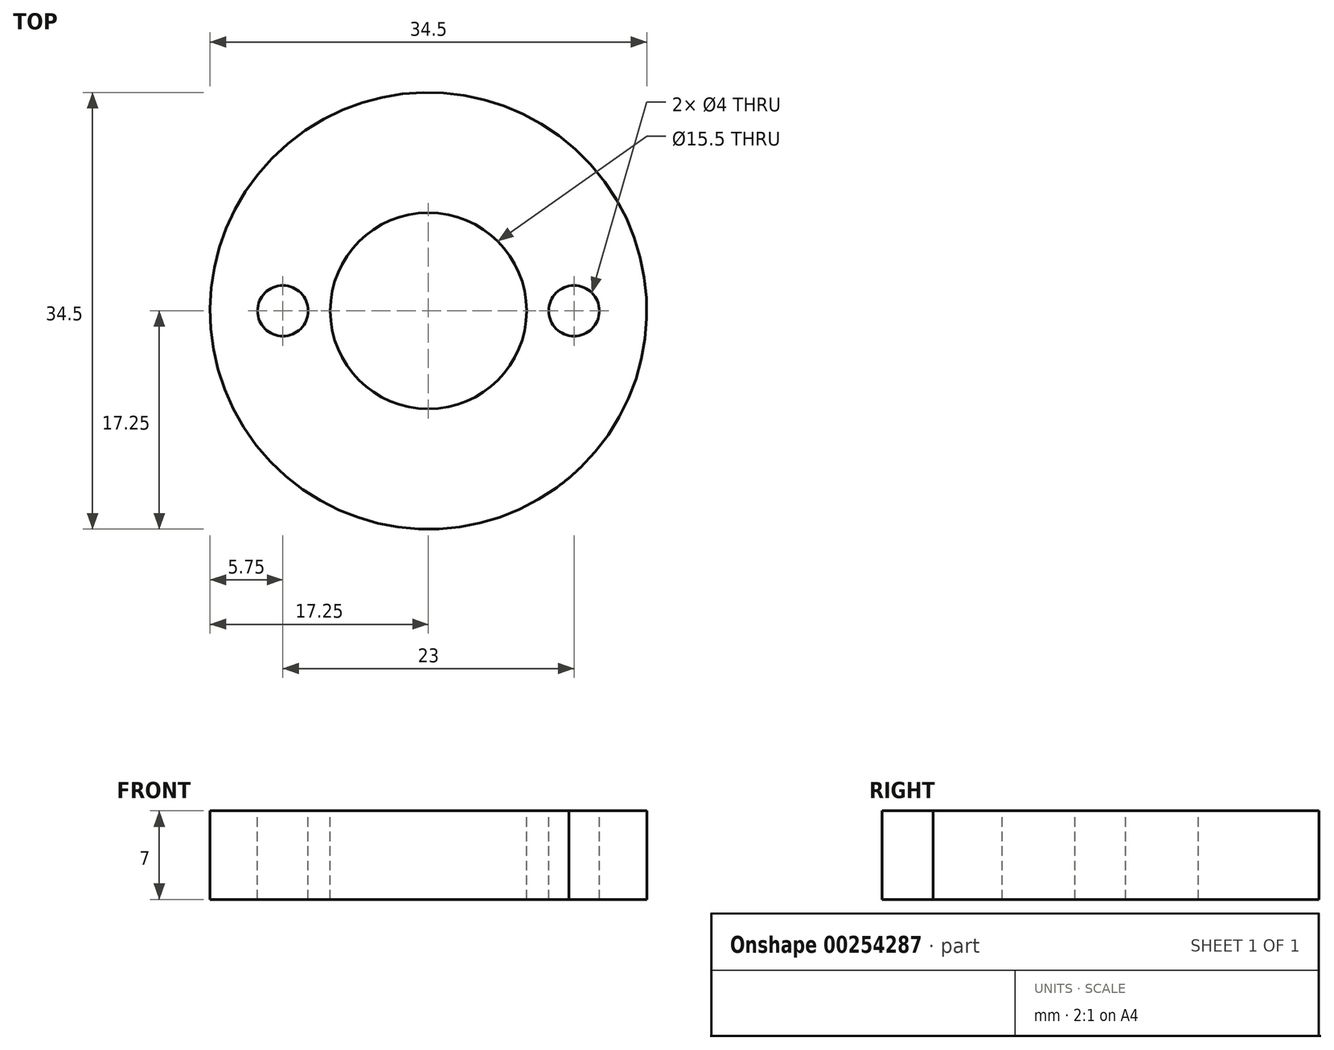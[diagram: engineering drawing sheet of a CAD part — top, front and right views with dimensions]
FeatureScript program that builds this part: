
annotation { "Feature Type Name" : "Feature", "Feature Type Description" : "" }
export const myFeature = defineFeature(function(context is Context, id is Id, definition is map)
    precondition{}
    {
        {
            var Q0;
            Q0=qCreatedBy(makeId("Top.planeOp"),FACE);
            var sketch = newSketch(context, id + "F0", { "sketchPlane" : qUnion([Q0])});
            skCircle(sketch, "E0", {"center": v(0, 0) * mm, "radius": 17.25 * mm});
            skLineSegment(sketch, "E1", {"start": v(0, 25.78) * mm, "end": v(0, -27.7) * mm});
            skLineSegment(sketch, "E2", {"start": v(-26.27, 0) * mm, "end": v(30.25, 0) * mm});
            skPoint(sketch, "E3.visualSharp", {"position": v(0, 20.27) * mm});
            skArc(sketch, "E3.filletArc", {"start": v(0.28, 19.56) * mm, "mid": v(0, 19.75) * mm, "end": v(-0.28, 19.56) * mm});
            skLineSegment(sketch, "E4", {"start": v(0, 17.25) * mm, "end": v(0, 19.75) * mm});
            skFitSpline(sketch, "E5", {"points": [v(-1.2, 17.2) * mm, v(-0.94, 18.19) * mm, v(-0.28, 19.56) * mm], "startDerivative": vector(0.47, 2.11) * mm, "endDerivative": vector(1.5, 2.4) * mm});
            skFitSpline(sketch, "E6.MirrorCS", {"points": [v(1.2, 17.2) * mm, v(0.94, 18.19) * mm, v(0.28, 19.56) * mm], "startDerivative": vector(-0.47, 2.11) * mm, "endDerivative": vector(-1.5, 2.4) * mm});
            skFitSpline(sketch, "E7", {"points": [v(-1.2, 17.2) * mm, v(0, 17.25) * mm, v(1.2, 17.2) * mm], "startDerivative": vector(2.41, 0.13) * mm, "endDerivative": vector(2.41, -0.13) * mm});
            skSolve(sketch);
        }
        {
            var Q0;
            {var subQ0=sQuery(id+"F0.wireOp",EDGE,"f5ca5393-df95-4c20-865a-a9dc07791ef0.31.0");Q0=makeQuery(id+"F0.imprint","IMPRINT",FACE,{"disambiguationData":[TD([[makeQuery(id+"F0.imprint","IMPRINT",EDGE,{"derivedFrom":subQ0}),-1.0]])]});}
            var Q1;
            {var subQ0=sQuery(id+"F0.wireOp",EDGE,"f5ca5393-df95-4c20-865a-a9dc07791ef0.29.0");Q1=makeQuery(id+"F0.imprint","IMPRINT",FACE,{"disambiguationData":[TD([[makeQuery(id+"F0.imprint","IMPRINT",EDGE,{"derivedFrom":subQ0}),-1.0]])]});}
            var Q2;
            {var subQ0=sQuery(id+"F0.wireOp",EDGE,"f5ca5393-df95-4c20-865a-a9dc07791ef0.30.0");Q2=makeQuery(id+"F0.imprint","IMPRINT",FACE,{"disambiguationData":[TD([[makeQuery(id+"F0.imprint","IMPRINT",EDGE,{"derivedFrom":subQ0}),-1.0]])]});}
            var Q3;
            {var subQ0=sQuery(id+"F0.wireOp",EDGE,"f5ca5393-df95-4c20-865a-a9dc07791ef0.32.0");Q3=makeQuery(id+"F0.imprint","IMPRINT",FACE,{"disambiguationData":[TD([[makeQuery(id+"F0.imprint","IMPRINT",EDGE,{"derivedFrom":subQ0}),-1.0]])]});}
            var Q4;
            {var subQ0=sQuery(id+"F0.wireOp",EDGE,"f5ca5393-df95-4c20-865a-a9dc07791ef0.33.0");Q4=makeQuery(id+"F0.imprint","IMPRINT",FACE,{"disambiguationData":[TD([[makeQuery(id+"F0.imprint","IMPRINT",EDGE,{"derivedFrom":subQ0}),-1.0]])]});}
            var Q5;
            {var subQ0=sQuery(id+"F0.wireOp",EDGE,"f5ca5393-df95-4c20-865a-a9dc07791ef0.34.0");Q5=makeQuery(id+"F0.imprint","IMPRINT",FACE,{"disambiguationData":[TD([[makeQuery(id+"F0.imprint","IMPRINT",EDGE,{"derivedFrom":subQ0}),-1.0]])]});}
            var Q6;
            {var subQ0=sQuery(id+"F0.wireOp",EDGE,"f5ca5393-df95-4c20-865a-a9dc07791ef0.17.0");Q6=makeQuery(id+"F0.imprint","IMPRINT",FACE,{"disambiguationData":[TD([[makeQuery(id+"F0.imprint","IMPRINT",EDGE,{"derivedFrom":subQ0}),-1.0]])]});}
            var Q7;
            {var subQ0=sQuery(id+"F0.wireOp",EDGE,"f5ca5393-df95-4c20-865a-a9dc07791ef0.35.0");Q7=makeQuery(id+"F0.imprint","IMPRINT",FACE,{"disambiguationData":[TD([[makeQuery(id+"F0.imprint","IMPRINT",EDGE,{"derivedFrom":subQ0}),-1.0]])]});}
            var Q8;
            {var subQ0=sQuery(id+"F0.wireOp",EDGE,"E0");var subQ8=makeQuery(id+"F0.imprint","INTERSECT",VERTEX,{"derivedFrom":[subQ0,sQuery(id+"F0.wireOp",EDGE,"5MArOXN8-ynDE-2cLv-vS9q-pv3LUURociim")]});Q8=makeQuery(id+"F0.imprint","IMPRINT",FACE,{"disambiguationData":[TD([[makeQuery(id+"F0.imprint","IMPRINT",EDGE,{"disambiguationData":[TD([[subQ8,1.0]])],"derivedFrom":subQ0}),1.0]])]});}
            var Q9;
            {var subQ0=sQuery(id+"F0.wireOp",EDGE,"fce4d2f8-0420-48c1-941b-f51cf35978c9.1.36.0");Q9=makeQuery(id+"F0.imprint","IMPRINT",FACE,{"disambiguationData":[TD([[makeQuery(id+"F0.imprint","IMPRINT",EDGE,{"derivedFrom":subQ0}),-1.0]])]});}
            var Q10;
            {var subQ0=sQuery(id+"F0.wireOp",EDGE,"f5ca5393-df95-4c20-865a-a9dc07791ef0.24.0");Q10=makeQuery(id+"F0.imprint","IMPRINT",FACE,{"disambiguationData":[TD([[makeQuery(id+"F0.imprint","IMPRINT",EDGE,{"derivedFrom":subQ0}),-1.0]])]});}
            var Q11;
            {var subQ0=sQuery(id+"F0.wireOp",EDGE,"fce4d2f8-0420-48c1-941b-f51cf35978c9.1.37.0");Q11=makeQuery(id+"F0.imprint","IMPRINT",FACE,{"disambiguationData":[TD([[makeQuery(id+"F0.imprint","IMPRINT",EDGE,{"derivedFrom":subQ0}),-1.0]])]});}
            var Q12;
            {var subQ0=sQuery(id+"F0.wireOp",EDGE,"f5ca5393-df95-4c20-865a-a9dc07791ef0.1.0");Q12=makeQuery(id+"F0.imprint","IMPRINT",FACE,{"disambiguationData":[TD([[makeQuery(id+"F0.imprint","IMPRINT",EDGE,{"derivedFrom":subQ0}),-1.0]])]});}
            var Q13;
            {var subQ0=sQuery(id+"F0.wireOp",EDGE,"f5ca5393-df95-4c20-865a-a9dc07791ef0.2.0");Q13=makeQuery(id+"F0.imprint","IMPRINT",FACE,{"disambiguationData":[TD([[makeQuery(id+"F0.imprint","IMPRINT",EDGE,{"derivedFrom":subQ0}),-1.0]])]});}
            var Q14;
            {var subQ0=sQuery(id+"F0.wireOp",EDGE,"f5ca5393-df95-4c20-865a-a9dc07791ef0.3.0");Q14=makeQuery(id+"F0.imprint","IMPRINT",FACE,{"disambiguationData":[TD([[makeQuery(id+"F0.imprint","IMPRINT",EDGE,{"derivedFrom":subQ0}),-1.0]])]});}
            var Q15;
            {var subQ0=sQuery(id+"F0.wireOp",EDGE,"E0");var subQ8=makeQuery(id+"F0.imprint","INTERSECT",VERTEX,{"derivedFrom":[subQ0,sQuery(id+"F0.wireOp",EDGE,"f5ca5393-df95-4c20-865a-a9dc07791ef0.10.2")]});Q15=makeQuery(id+"F0.imprint","IMPRINT",FACE,{"disambiguationData":[TD([[makeQuery(id+"F0.imprint","IMPRINT",EDGE,{"disambiguationData":[TD([[subQ8,1.0]])],"derivedFrom":subQ0}),1.0]])]});}
            var Q16;
            {var subQ0=sQuery(id+"F0.wireOp",EDGE,"f5ca5393-df95-4c20-865a-a9dc07791ef0.18.0");Q16=makeQuery(id+"F0.imprint","IMPRINT",FACE,{"disambiguationData":[TD([[makeQuery(id+"F0.imprint","IMPRINT",EDGE,{"derivedFrom":subQ0}),-1.0]])]});}
            var Q17;
            {var subQ0=sQuery(id+"F0.wireOp",EDGE,"f5ca5393-df95-4c20-865a-a9dc07791ef0.22.0");Q17=makeQuery(id+"F0.imprint","IMPRINT",FACE,{"disambiguationData":[TD([[makeQuery(id+"F0.imprint","IMPRINT",EDGE,{"derivedFrom":subQ0}),-1.0]])]});}
            var Q18;
            {var subQ0=sQuery(id+"F0.wireOp",EDGE,"f5ca5393-df95-4c20-865a-a9dc07791ef0.4.0");Q18=makeQuery(id+"F0.imprint","IMPRINT",FACE,{"disambiguationData":[TD([[makeQuery(id+"F0.imprint","IMPRINT",EDGE,{"derivedFrom":subQ0}),-1.0]])]});}
            var Q19;
            {var subQ0=sQuery(id+"F0.wireOp",EDGE,"E0");var subQ8=makeQuery(id+"F0.imprint","INTERSECT",VERTEX,{"derivedFrom":[subQ0,sQuery(id+"F0.wireOp",EDGE,"f5ca5393-df95-4c20-865a-a9dc07791ef0.19.0")]});Q19=makeQuery(id+"F0.imprint","IMPRINT",FACE,{"disambiguationData":[TD([[makeQuery(id+"F0.imprint","IMPRINT",EDGE,{"disambiguationData":[TD([[subQ8,1.0]])],"derivedFrom":subQ0}),1.0]])]});}
            var Q20;
            {var subQ0=sQuery(id+"F0.wireOp",EDGE,"f5ca5393-df95-4c20-865a-a9dc07791ef0.20.0");Q20=makeQuery(id+"F0.imprint","IMPRINT",FACE,{"disambiguationData":[TD([[makeQuery(id+"F0.imprint","IMPRINT",EDGE,{"derivedFrom":subQ0}),-1.0]])]});}
            var Q21;
            {var subQ0=sQuery(id+"F0.wireOp",EDGE,"f5ca5393-df95-4c20-865a-a9dc07791ef0.23.0");Q21=makeQuery(id+"F0.imprint","IMPRINT",FACE,{"disambiguationData":[TD([[makeQuery(id+"F0.imprint","IMPRINT",EDGE,{"derivedFrom":subQ0}),-1.0]])]});}
            var Q22;
            {var subQ0=sQuery(id+"F0.wireOp",EDGE,"f5ca5393-df95-4c20-865a-a9dc07791ef0.21.0");Q22=makeQuery(id+"F0.imprint","IMPRINT",FACE,{"disambiguationData":[TD([[makeQuery(id+"F0.imprint","IMPRINT",EDGE,{"derivedFrom":subQ0}),-1.0]])]});}
            var Q23;
            {var subQ0=sQuery(id+"F0.wireOp",EDGE,"f5ca5393-df95-4c20-865a-a9dc07791ef0.19.0");Q23=makeQuery(id+"F0.imprint","IMPRINT",FACE,{"disambiguationData":[TD([[makeQuery(id+"F0.imprint","IMPRINT",EDGE,{"derivedFrom":subQ0}),-1.0]])]});}
            var Q24;
            {var subQ0=sQuery(id+"F0.wireOp",EDGE,"f5ca5393-df95-4c20-865a-a9dc07791ef0.15.0");Q24=makeQuery(id+"F0.imprint","IMPRINT",FACE,{"disambiguationData":[TD([[makeQuery(id+"F0.imprint","IMPRINT",EDGE,{"derivedFrom":subQ0}),-1.0]])]});}
            var Q25;
            {var subQ0=sQuery(id+"F0.wireOp",EDGE,"f5ca5393-df95-4c20-865a-a9dc07791ef0.25.0");Q25=makeQuery(id+"F0.imprint","IMPRINT",FACE,{"disambiguationData":[TD([[makeQuery(id+"F0.imprint","IMPRINT",EDGE,{"derivedFrom":subQ0}),-1.0]])]});}
            var Q26;
            {var subQ0=sQuery(id+"F0.wireOp",EDGE,"f5ca5393-df95-4c20-865a-a9dc07791ef0.8.0");Q26=makeQuery(id+"F0.imprint","IMPRINT",FACE,{"disambiguationData":[TD([[makeQuery(id+"F0.imprint","IMPRINT",EDGE,{"derivedFrom":subQ0}),-1.0]])]});}
            var Q27;
            {var subQ0=sQuery(id+"F0.wireOp",EDGE,"f5ca5393-df95-4c20-865a-a9dc07791ef0.9.0");Q27=makeQuery(id+"F0.imprint","IMPRINT",FACE,{"disambiguationData":[TD([[makeQuery(id+"F0.imprint","IMPRINT",EDGE,{"derivedFrom":subQ0}),-1.0]])]});}
            var Q28;
            {var subQ0=sQuery(id+"F0.wireOp",EDGE,"f5ca5393-df95-4c20-865a-a9dc07791ef0.26.0");Q28=makeQuery(id+"F0.imprint","IMPRINT",FACE,{"disambiguationData":[TD([[makeQuery(id+"F0.imprint","IMPRINT",EDGE,{"derivedFrom":subQ0}),-1.0]])]});}
            var Q29;
            {var subQ0=sQuery(id+"F0.wireOp",EDGE,"f5ca5393-df95-4c20-865a-a9dc07791ef0.10.0");Q29=makeQuery(id+"F0.imprint","IMPRINT",FACE,{"disambiguationData":[TD([[makeQuery(id+"F0.imprint","IMPRINT",EDGE,{"derivedFrom":subQ0}),-1.0]])]});}
            var Q30;
            {var subQ0=sQuery(id+"F0.wireOp",EDGE,"f5ca5393-df95-4c20-865a-a9dc07791ef0.27.0");Q30=makeQuery(id+"F0.imprint","IMPRINT",FACE,{"disambiguationData":[TD([[makeQuery(id+"F0.imprint","IMPRINT",EDGE,{"derivedFrom":subQ0}),-1.0]])]});}
            var Q31;
            {var subQ0=sQuery(id+"F0.wireOp",EDGE,"f5ca5393-df95-4c20-865a-a9dc07791ef0.11.0");Q31=makeQuery(id+"F0.imprint","IMPRINT",FACE,{"disambiguationData":[TD([[makeQuery(id+"F0.imprint","IMPRINT",EDGE,{"derivedFrom":subQ0}),-1.0]])]});}
            var Q32;
            {var subQ0=sQuery(id+"F0.wireOp",EDGE,"f5ca5393-df95-4c20-865a-a9dc07791ef0.28.0");Q32=makeQuery(id+"F0.imprint","IMPRINT",FACE,{"disambiguationData":[TD([[makeQuery(id+"F0.imprint","IMPRINT",EDGE,{"derivedFrom":subQ0}),-1.0]])]});}
            var Q33;
            {var subQ0=sQuery(id+"F0.wireOp",EDGE,"f5ca5393-df95-4c20-865a-a9dc07791ef0.12.0");Q33=makeQuery(id+"F0.imprint","IMPRINT",FACE,{"disambiguationData":[TD([[makeQuery(id+"F0.imprint","IMPRINT",EDGE,{"derivedFrom":subQ0}),-1.0]])]});}
            var Q34;
            {var subQ0=sQuery(id+"F0.wireOp",EDGE,"pMwcg0If-iJ5C-wkS0-yKET-ZU3b9yseXKQn");Q34=makeQuery(id+"F0.imprint","IMPRINT",FACE,{"disambiguationData":[TD([[makeQuery(id+"F0.imprint","IMPRINT",EDGE,{"derivedFrom":subQ0}),-1.0]])]});}
            var Q35;
            {var subQ0=sQuery(id+"F0.wireOp",EDGE,"f5ca5393-df95-4c20-865a-a9dc07791ef0.13.0");Q35=makeQuery(id+"F0.imprint","IMPRINT",FACE,{"disambiguationData":[TD([[makeQuery(id+"F0.imprint","IMPRINT",EDGE,{"derivedFrom":subQ0}),-1.0]])]});}
            var Q36;
            {var subQ0=sQuery(id+"F0.wireOp",EDGE,"5MArOXN8-ynDE-2cLv-vS9q-pv3LUURociim");Q36=makeQuery(id+"F0.imprint","IMPRINT",FACE,{"disambiguationData":[TD([[makeQuery(id+"F0.imprint","IMPRINT",EDGE,{"derivedFrom":subQ0}),-1.0]])]});}
            var Q37;
            {var subQ0=sQuery(id+"F0.wireOp",EDGE,"E0");var subQ8=makeQuery(id+"F0.imprint","INTERSECT",VERTEX,{"derivedFrom":[subQ0,sQuery(id+"F0.wireOp",EDGE,"f5ca5393-df95-4c20-865a-a9dc07791ef0.29.2")]});Q37=makeQuery(id+"F0.imprint","IMPRINT",FACE,{"disambiguationData":[TD([[makeQuery(id+"F0.imprint","IMPRINT",EDGE,{"disambiguationData":[TD([[subQ8,1.0]])],"derivedFrom":subQ0}),1.0]])]});}
            var Q38;
            {var subQ0=sQuery(id+"F0.wireOp",EDGE,"f5ca5393-df95-4c20-865a-a9dc07791ef0.16.0");Q38=makeQuery(id+"F0.imprint","IMPRINT",FACE,{"disambiguationData":[TD([[makeQuery(id+"F0.imprint","IMPRINT",EDGE,{"derivedFrom":subQ0}),-1.0]])]});}
            var Q39;
            {var subQ0=sQuery(id+"F0.wireOp",EDGE,"f5ca5393-df95-4c20-865a-a9dc07791ef0.19.2");Q39=makeQuery(id+"F0.imprint","IMPRINT",FACE,{"disambiguationData":[TD([[makeQuery(id+"F0.imprint","IMPRINT",EDGE,{"derivedFrom":subQ0}),-1.0]])]});}
            var Q40;
            {var subQ0=sQuery(id+"F0.wireOp",EDGE,"f5ca5393-df95-4c20-865a-a9dc07791ef0.14.0");Q40=makeQuery(id+"F0.imprint","IMPRINT",FACE,{"disambiguationData":[TD([[makeQuery(id+"F0.imprint","IMPRINT",EDGE,{"derivedFrom":subQ0}),-1.0]])]});}
            var Q41;
            {var subQ0=sQuery(id+"F0.wireOp",EDGE,"f5ca5393-df95-4c20-865a-a9dc07791ef0.7.0");Q41=makeQuery(id+"F0.imprint","IMPRINT",FACE,{"disambiguationData":[TD([[makeQuery(id+"F0.imprint","IMPRINT",EDGE,{"derivedFrom":subQ0}),-1.0]])]});}
            var Q42;
            {var subQ0=sQuery(id+"F0.wireOp",EDGE,"f5ca5393-df95-4c20-865a-a9dc07791ef0.5.0");Q42=makeQuery(id+"F0.imprint","IMPRINT",FACE,{"disambiguationData":[TD([[makeQuery(id+"F0.imprint","IMPRINT",EDGE,{"derivedFrom":subQ0}),-1.0]])]});}
            var Q43;
            {var subQ0=sQuery(id+"F0.wireOp",EDGE,"f5ca5393-df95-4c20-865a-a9dc07791ef0.6.0");Q43=makeQuery(id+"F0.imprint","IMPRINT",FACE,{"disambiguationData":[TD([[makeQuery(id+"F0.imprint","IMPRINT",EDGE,{"derivedFrom":subQ0}),-1.0]])]});}
            var Q44;
            {var subQ0=sQuery(id+"F0.wireOp",EDGE,"f5ca5393-df95-4c20-865a-a9dc07791ef0.27.2");Q44=makeQuery(id+"F0.imprint","IMPRINT",FACE,{"disambiguationData":[TD([[makeQuery(id+"F0.imprint","IMPRINT",EDGE,{"derivedFrom":subQ0}),-1.0]])]});}
            var Q45;
            {var subQ0=sQuery(id+"F0.wireOp",EDGE,"f5ca5393-df95-4c20-865a-a9dc07791ef0.9.2");Q45=makeQuery(id+"F0.imprint","IMPRINT",FACE,{"disambiguationData":[TD([[makeQuery(id+"F0.imprint","IMPRINT",EDGE,{"derivedFrom":subQ0}),-1.0]])]});}
            var Q46;
            {var subQ0=sQuery(id+"F0.wireOp",EDGE,"f5ca5393-df95-4c20-865a-a9dc07791ef0.18.2");Q46=makeQuery(id+"F0.imprint","IMPRINT",FACE,{"disambiguationData":[TD([[makeQuery(id+"F0.imprint","IMPRINT",EDGE,{"derivedFrom":subQ0}),-1.0]])]});}
            var Q47;
            {var subQ1=sQuery(id+"F0.wireOp",EDGE,"E0");var subQ3=sQuery(id+"F0.wireOp",EDGE,"E2");var subQ4=makeQuery(id+"F0.imprint","INTERSECT",VERTEX,{"disambiguationData":[OD(1.0)],"derivedFrom":[subQ1,subQ3]});Q47=makeQuery(id+"F0.imprint","IMPRINT",FACE,{"disambiguationData":[TD([[makeQuery(id+"F0.imprint","IMPRINT",EDGE,{"disambiguationData":[TD([[subQ4,-1.0]])],"derivedFrom":subQ3}),1.0]])]});}
            var Q48;
            {var subQ1=sQuery(id+"F0.wireOp",EDGE,"E0");var subQ3=sQuery(id+"F0.wireOp",EDGE,"E2");var subQ4=makeQuery(id+"F0.imprint","INTERSECT",VERTEX,{"disambiguationData":[OD(0.0)],"derivedFrom":[subQ1,subQ3]});Q48=makeQuery(id+"F0.imprint","IMPRINT",FACE,{"disambiguationData":[TD([[makeQuery(id+"F0.imprint","IMPRINT",EDGE,{"disambiguationData":[TD([[subQ4,1.0]])],"derivedFrom":subQ3}),1.0]])]});}
            var Q49;
            {var subQ1=sQuery(id+"F0.wireOp",EDGE,"E4");Q49=makeQuery(id+"F0.imprint","IMPRINT",FACE,{"disambiguationData":[TD([[makeQuery(id+"F0.imprint","IMPRINT",EDGE,{"derivedFrom":subQ1}),-1.0]])]});}
            var Q50;
            {var subQ1=sQuery(id+"F0.wireOp",EDGE,"E4");Q50=makeQuery(id+"F0.imprint","IMPRINT",FACE,{"disambiguationData":[TD([[makeQuery(id+"F0.imprint","IMPRINT",EDGE,{"derivedFrom":subQ1}),1.0]])]});}
            extrude(context, id + "F1", {"entities" : qUnion([Q0, Q1, Q2, Q3, Q4, Q5, Q6, Q7, Q8, Q9, Q10, Q11, Q12, Q13, Q14, Q15, Q16, Q17, Q18, Q19, Q20, Q21, Q22, Q23, Q24, Q25, Q26, Q27, Q28, Q29, Q30, Q31, Q32, Q33, Q34, Q35, Q36, Q37, Q38, Q39, Q40, Q41, Q42, Q43, Q44, Q45, Q46, Q47, Q48, Q49, Q50]), "depth" : 7 * mm, "offsetDistance" : 25 * mm});
        }
        {
            var Q0;
            Q0=makeQuery(id+"F1.opExtrude","CAP_FACE",FACE,{"disambiguationData":[OSD([sQuery(id+"F0.wireOp",EDGE,"E0"),sQuery(id+"F0.wireOp",EDGE,"5MArOXN8-ynDE-2cLv-vS9q-pv3LUURociim"),sQuery(id+"F0.wireOp",EDGE,"pMwcg0If-iJ5C-wkS0-yKET-ZU3b9yseXKQn"),sQuery(id+"F0.wireOp",EDGE,"E3.filletArc"),sQuery(id+"F0.wireOp",EDGE,"f5ca5393-df95-4c20-865a-a9dc07791ef0.1.0"),sQuery(id+"F0.wireOp",EDGE,"f5ca5393-df95-4c20-865a-a9dc07791ef0.1.1"),sQuery(id+"F0.wireOp",EDGE,"f5ca5393-df95-4c20-865a-a9dc07791ef0.1.2"),sQuery(id+"F0.wireOp",EDGE,"f5ca5393-df95-4c20-865a-a9dc07791ef0.2.0"),sQuery(id+"F0.wireOp",EDGE,"f5ca5393-df95-4c20-865a-a9dc07791ef0.2.1"),sQuery(id+"F0.wireOp",EDGE,"f5ca5393-df95-4c20-865a-a9dc07791ef0.2.2"),sQuery(id+"F0.wireOp",EDGE,"f5ca5393-df95-4c20-865a-a9dc07791ef0.3.0"),sQuery(id+"F0.wireOp",EDGE,"f5ca5393-df95-4c20-865a-a9dc07791ef0.3.1"),sQuery(id+"F0.wireOp",EDGE,"f5ca5393-df95-4c20-865a-a9dc07791ef0.3.2"),sQuery(id+"F0.wireOp",EDGE,"f5ca5393-df95-4c20-865a-a9dc07791ef0.4.0"),sQuery(id+"F0.wireOp",EDGE,"f5ca5393-df95-4c20-865a-a9dc07791ef0.4.1"),sQuery(id+"F0.wireOp",EDGE,"f5ca5393-df95-4c20-865a-a9dc07791ef0.4.2"),sQuery(id+"F0.wireOp",EDGE,"f5ca5393-df95-4c20-865a-a9dc07791ef0.5.0"),sQuery(id+"F0.wireOp",EDGE,"f5ca5393-df95-4c20-865a-a9dc07791ef0.5.1"),sQuery(id+"F0.wireOp",EDGE,"f5ca5393-df95-4c20-865a-a9dc07791ef0.5.2"),sQuery(id+"F0.wireOp",EDGE,"f5ca5393-df95-4c20-865a-a9dc07791ef0.6.0"),sQuery(id+"F0.wireOp",EDGE,"f5ca5393-df95-4c20-865a-a9dc07791ef0.6.1"),sQuery(id+"F0.wireOp",EDGE,"f5ca5393-df95-4c20-865a-a9dc07791ef0.6.2"),sQuery(id+"F0.wireOp",EDGE,"f5ca5393-df95-4c20-865a-a9dc07791ef0.7.0"),sQuery(id+"F0.wireOp",EDGE,"f5ca5393-df95-4c20-865a-a9dc07791ef0.7.1"),sQuery(id+"F0.wireOp",EDGE,"f5ca5393-df95-4c20-865a-a9dc07791ef0.7.2"),sQuery(id+"F0.wireOp",EDGE,"f5ca5393-df95-4c20-865a-a9dc07791ef0.8.0"),sQuery(id+"F0.wireOp",EDGE,"f5ca5393-df95-4c20-865a-a9dc07791ef0.8.1"),sQuery(id+"F0.wireOp",EDGE,"f5ca5393-df95-4c20-865a-a9dc07791ef0.8.2"),sQuery(id+"F0.wireOp",EDGE,"f5ca5393-df95-4c20-865a-a9dc07791ef0.9.0"),sQuery(id+"F0.wireOp",EDGE,"f5ca5393-df95-4c20-865a-a9dc07791ef0.9.1"),sQuery(id+"F0.wireOp",EDGE,"f5ca5393-df95-4c20-865a-a9dc07791ef0.9.2"),sQuery(id+"F0.wireOp",EDGE,"f5ca5393-df95-4c20-865a-a9dc07791ef0.10.0"),sQuery(id+"F0.wireOp",EDGE,"f5ca5393-df95-4c20-865a-a9dc07791ef0.10.1"),sQuery(id+"F0.wireOp",EDGE,"f5ca5393-df95-4c20-865a-a9dc07791ef0.10.2"),sQuery(id+"F0.wireOp",EDGE,"f5ca5393-df95-4c20-865a-a9dc07791ef0.11.0"),sQuery(id+"F0.wireOp",EDGE,"f5ca5393-df95-4c20-865a-a9dc07791ef0.11.1"),sQuery(id+"F0.wireOp",EDGE,"f5ca5393-df95-4c20-865a-a9dc07791ef0.11.2"),sQuery(id+"F0.wireOp",EDGE,"f5ca5393-df95-4c20-865a-a9dc07791ef0.12.0"),sQuery(id+"F0.wireOp",EDGE,"f5ca5393-df95-4c20-865a-a9dc07791ef0.12.1"),sQuery(id+"F0.wireOp",EDGE,"f5ca5393-df95-4c20-865a-a9dc07791ef0.12.2"),sQuery(id+"F0.wireOp",EDGE,"f5ca5393-df95-4c20-865a-a9dc07791ef0.13.0"),sQuery(id+"F0.wireOp",EDGE,"f5ca5393-df95-4c20-865a-a9dc07791ef0.13.1"),sQuery(id+"F0.wireOp",EDGE,"f5ca5393-df95-4c20-865a-a9dc07791ef0.13.2"),sQuery(id+"F0.wireOp",EDGE,"f5ca5393-df95-4c20-865a-a9dc07791ef0.14.0"),sQuery(id+"F0.wireOp",EDGE,"f5ca5393-df95-4c20-865a-a9dc07791ef0.14.1"),sQuery(id+"F0.wireOp",EDGE,"f5ca5393-df95-4c20-865a-a9dc07791ef0.14.2"),sQuery(id+"F0.wireOp",EDGE,"f5ca5393-df95-4c20-865a-a9dc07791ef0.15.0"),sQuery(id+"F0.wireOp",EDGE,"f5ca5393-df95-4c20-865a-a9dc07791ef0.15.1"),sQuery(id+"F0.wireOp",EDGE,"f5ca5393-df95-4c20-865a-a9dc07791ef0.15.2"),sQuery(id+"F0.wireOp",EDGE,"f5ca5393-df95-4c20-865a-a9dc07791ef0.16.0"),sQuery(id+"F0.wireOp",EDGE,"f5ca5393-df95-4c20-865a-a9dc07791ef0.16.1"),sQuery(id+"F0.wireOp",EDGE,"f5ca5393-df95-4c20-865a-a9dc07791ef0.16.2"),sQuery(id+"F0.wireOp",EDGE,"f5ca5393-df95-4c20-865a-a9dc07791ef0.17.0"),sQuery(id+"F0.wireOp",EDGE,"f5ca5393-df95-4c20-865a-a9dc07791ef0.17.1"),sQuery(id+"F0.wireOp",EDGE,"f5ca5393-df95-4c20-865a-a9dc07791ef0.17.2"),sQuery(id+"F0.wireOp",EDGE,"f5ca5393-df95-4c20-865a-a9dc07791ef0.18.0"),sQuery(id+"F0.wireOp",EDGE,"f5ca5393-df95-4c20-865a-a9dc07791ef0.18.1"),sQuery(id+"F0.wireOp",EDGE,"f5ca5393-df95-4c20-865a-a9dc07791ef0.18.2"),sQuery(id+"F0.wireOp",EDGE,"f5ca5393-df95-4c20-865a-a9dc07791ef0.19.0"),sQuery(id+"F0.wireOp",EDGE,"f5ca5393-df95-4c20-865a-a9dc07791ef0.19.1"),sQuery(id+"F0.wireOp",EDGE,"f5ca5393-df95-4c20-865a-a9dc07791ef0.19.2"),sQuery(id+"F0.wireOp",EDGE,"f5ca5393-df95-4c20-865a-a9dc07791ef0.20.0"),sQuery(id+"F0.wireOp",EDGE,"f5ca5393-df95-4c20-865a-a9dc07791ef0.20.1"),sQuery(id+"F0.wireOp",EDGE,"f5ca5393-df95-4c20-865a-a9dc07791ef0.20.2"),sQuery(id+"F0.wireOp",EDGE,"f5ca5393-df95-4c20-865a-a9dc07791ef0.21.0"),sQuery(id+"F0.wireOp",EDGE,"f5ca5393-df95-4c20-865a-a9dc07791ef0.21.1"),sQuery(id+"F0.wireOp",EDGE,"f5ca5393-df95-4c20-865a-a9dc07791ef0.21.2"),sQuery(id+"F0.wireOp",EDGE,"f5ca5393-df95-4c20-865a-a9dc07791ef0.22.0"),sQuery(id+"F0.wireOp",EDGE,"f5ca5393-df95-4c20-865a-a9dc07791ef0.22.1"),sQuery(id+"F0.wireOp",EDGE,"f5ca5393-df95-4c20-865a-a9dc07791ef0.22.2"),sQuery(id+"F0.wireOp",EDGE,"f5ca5393-df95-4c20-865a-a9dc07791ef0.23.0"),sQuery(id+"F0.wireOp",EDGE,"f5ca5393-df95-4c20-865a-a9dc07791ef0.23.1"),sQuery(id+"F0.wireOp",EDGE,"f5ca5393-df95-4c20-865a-a9dc07791ef0.23.2"),sQuery(id+"F0.wireOp",EDGE,"f5ca5393-df95-4c20-865a-a9dc07791ef0.24.0"),sQuery(id+"F0.wireOp",EDGE,"f5ca5393-df95-4c20-865a-a9dc07791ef0.24.1"),sQuery(id+"F0.wireOp",EDGE,"f5ca5393-df95-4c20-865a-a9dc07791ef0.24.2"),sQuery(id+"F0.wireOp",EDGE,"f5ca5393-df95-4c20-865a-a9dc07791ef0.25.0"),sQuery(id+"F0.wireOp",EDGE,"f5ca5393-df95-4c20-865a-a9dc07791ef0.25.1"),sQuery(id+"F0.wireOp",EDGE,"f5ca5393-df95-4c20-865a-a9dc07791ef0.25.2"),sQuery(id+"F0.wireOp",EDGE,"f5ca5393-df95-4c20-865a-a9dc07791ef0.26.0"),sQuery(id+"F0.wireOp",EDGE,"f5ca5393-df95-4c20-865a-a9dc07791ef0.26.1"),sQuery(id+"F0.wireOp",EDGE,"f5ca5393-df95-4c20-865a-a9dc07791ef0.26.2"),sQuery(id+"F0.wireOp",EDGE,"f5ca5393-df95-4c20-865a-a9dc07791ef0.27.0"),sQuery(id+"F0.wireOp",EDGE,"f5ca5393-df95-4c20-865a-a9dc07791ef0.27.1"),sQuery(id+"F0.wireOp",EDGE,"f5ca5393-df95-4c20-865a-a9dc07791ef0.27.2"),sQuery(id+"F0.wireOp",EDGE,"f5ca5393-df95-4c20-865a-a9dc07791ef0.28.0"),sQuery(id+"F0.wireOp",EDGE,"f5ca5393-df95-4c20-865a-a9dc07791ef0.28.1"),sQuery(id+"F0.wireOp",EDGE,"f5ca5393-df95-4c20-865a-a9dc07791ef0.28.2"),sQuery(id+"F0.wireOp",EDGE,"f5ca5393-df95-4c20-865a-a9dc07791ef0.29.0"),sQuery(id+"F0.wireOp",EDGE,"f5ca5393-df95-4c20-865a-a9dc07791ef0.29.1"),sQuery(id+"F0.wireOp",EDGE,"f5ca5393-df95-4c20-865a-a9dc07791ef0.29.2"),sQuery(id+"F0.wireOp",EDGE,"f5ca5393-df95-4c20-865a-a9dc07791ef0.30.0"),sQuery(id+"F0.wireOp",EDGE,"f5ca5393-df95-4c20-865a-a9dc07791ef0.30.1"),sQuery(id+"F0.wireOp",EDGE,"f5ca5393-df95-4c20-865a-a9dc07791ef0.30.2"),sQuery(id+"F0.wireOp",EDGE,"f5ca5393-df95-4c20-865a-a9dc07791ef0.31.0"),sQuery(id+"F0.wireOp",EDGE,"f5ca5393-df95-4c20-865a-a9dc07791ef0.31.1"),sQuery(id+"F0.wireOp",EDGE,"f5ca5393-df95-4c20-865a-a9dc07791ef0.31.2"),sQuery(id+"F0.wireOp",EDGE,"f5ca5393-df95-4c20-865a-a9dc07791ef0.32.0"),sQuery(id+"F0.wireOp",EDGE,"f5ca5393-df95-4c20-865a-a9dc07791ef0.32.1"),sQuery(id+"F0.wireOp",EDGE,"f5ca5393-df95-4c20-865a-a9dc07791ef0.32.2"),sQuery(id+"F0.wireOp",EDGE,"f5ca5393-df95-4c20-865a-a9dc07791ef0.33.0"),sQuery(id+"F0.wireOp",EDGE,"f5ca5393-df95-4c20-865a-a9dc07791ef0.33.1"),sQuery(id+"F0.wireOp",EDGE,"f5ca5393-df95-4c20-865a-a9dc07791ef0.33.2"),sQuery(id+"F0.wireOp",EDGE,"f5ca5393-df95-4c20-865a-a9dc07791ef0.34.0"),sQuery(id+"F0.wireOp",EDGE,"f5ca5393-df95-4c20-865a-a9dc07791ef0.34.1"),sQuery(id+"F0.wireOp",EDGE,"f5ca5393-df95-4c20-865a-a9dc07791ef0.34.2"),sQuery(id+"F0.wireOp",EDGE,"f5ca5393-df95-4c20-865a-a9dc07791ef0.35.0"),sQuery(id+"F0.wireOp",EDGE,"f5ca5393-df95-4c20-865a-a9dc07791ef0.35.1"),sQuery(id+"F0.wireOp",EDGE,"f5ca5393-df95-4c20-865a-a9dc07791ef0.35.2"),sQuery(id+"F0.wireOp",EDGE,"fce4d2f8-0420-48c1-941b-f51cf35978c9.1.36.0"),sQuery(id+"F0.wireOp",EDGE,"fce4d2f8-0420-48c1-941b-f51cf35978c9.3.36.0"),sQuery(id+"F0.wireOp",EDGE,"fce4d2f8-0420-48c1-941b-f51cf35978c9.7.36.0"),sQuery(id+"F0.wireOp",EDGE,"fce4d2f8-0420-48c1-941b-f51cf35978c9.1.37.0"),sQuery(id+"F0.wireOp",EDGE,"fce4d2f8-0420-48c1-941b-f51cf35978c9.3.37.0"),sQuery(id+"F0.wireOp",EDGE,"fce4d2f8-0420-48c1-941b-f51cf35978c9.7.37.0")])],"isStart":false});
            var sketch = newSketch(context, id + "F2", { "sketchPlane" : qUnion([Q0])});
            skCircle(sketch, "E8", {"center": v(0, 0) * mm, "radius": 7.75 * mm});
            skSolve(sketch);
        }
        {
            var Q0;
            Q0 = qSketchRegion(id + "F2", true);
            extrude(context, id + "F3", {"entities" : qUnion([Q0]), "operationType" : NewBodyOperationType.REMOVE, "oppositeDirection" : true, "depth" : 25 * mm, "offsetDistance" : 25 * mm, "symmetric" : true});
        }
        {
            var Q0;
            Q0=qCreatedBy(makeId("Top.planeOp"),FACE);
            cPlane(context, id + "F4", {"entities" : qUnion([Q0]), "cplaneType" : CPlaneType.OFFSET, "offset" : 3.5 * mm, "width" : 150 * mm, "height" : 150 * mm});
        }
        {
            var Q0;
            Q0=qCreatedBy(id+"F4.planeOp",FACE);
            var sketch = newSketch(context, id + "F5", { "sketchPlane" : qUnion([Q0])});
            skCircle(sketch, "E9", {"center": v(0, 0) * mm, "radius": 18.75 * mm});
            skSolve(sketch);
        }
        {
            var Q0;
            Q0=qCreatedBy(makeId("Front.planeOp"),FACE);
            var sketch = newSketch(context, id + "F6", { "sketchPlane" : qUnion([Q0])});
            skLineSegment(sketch, "E10", {"start": v(0, -8.54) * mm, "end": v(0, 21.05) * mm});
            skLineSegment(sketch, "E11.0", {"start": v(19.75, 0) * mm, "end": v(19.75, 7) * mm});
            skLineSegment(sketch, "E12.0", {"start": v(-19, 0) * mm, "end": v(19.75, 0) * mm});
            skLineSegment(sketch, "E13.MirrorCS", {"start": v(-19, 7) * mm, "end": v(19.75, 7) * mm});
            skLineSegment(sketch, "E14", {"start": v(19.75, 3.5) * mm, "end": v(18.75, 3.5) * mm});
            skArc(sketch, "E15", {"start": v(19.75, 7) * mm, "mid": v(18.75, 3.5) * mm, "end": v(19.75, 0) * mm});
            skLineSegment(sketch, "E16", {"start": v(19.75, 0) * mm, "end": v(21.4, 0) * mm});
            skLineSegment(sketch, "E17", {"start": v(21.4, 0) * mm, "end": v(21.4, 7) * mm});
            skLineSegment(sketch, "E18", {"start": v(19.75, 7) * mm, "end": v(21.4, 7) * mm});
            skSolve(sketch);
        }
        {
            var Q0;
            {var subQ3=sQuery(id+"F6.wireOp",EDGE,"E14");Q0=makeQuery(id+"F6.imprint","IMPRINT",FACE,{"disambiguationData":[TD([[makeQuery(id+"F6.imprint","IMPRINT",EDGE,{"derivedFrom":subQ3}),-1.0]])]});}
            var Q1;
            {var subQ0=sQuery(id+"F6.wireOp",EDGE,"E16");Q1=makeQuery(id+"F6.imprint","IMPRINT",FACE,{"disambiguationData":[TD([[makeQuery(id+"F6.imprint","IMPRINT",EDGE,{"derivedFrom":subQ0}),1.0]])]});}
            var Q2;
            {var subQ3=sQuery(id+"F6.wireOp",EDGE,"E14");Q2=makeQuery(id+"F6.imprint","IMPRINT",FACE,{"disambiguationData":[TD([[makeQuery(id+"F6.imprint","IMPRINT",EDGE,{"derivedFrom":subQ3}),1.0]])]});}
            var Q3;
            Q3=sQuery(id+"F5.wireOp",EDGE,"E9");
            sweep(context, id + "F7", {"operationType" : NewBodyOperationType.REMOVE, "profiles" : qUnion([Q0, Q1, Q2]), "path" : qUnion([Q3])});
        }
        {
            var Q0;
            Q0=qCreatedBy(makeId("Right.planeOp"),FACE);
            var sketch = newSketch(context, id + "F8", { "sketchPlane" : qUnion([Q0])});
            skLineSegment(sketch, "E19", {"start": v(0, 0) * mm, "end": v(0, 24.18) * mm});
            skSolve(sketch);
        }
        {
            var Q0;
            Q0=makeQuery(id+"F1.opExtrude","SWEPT_BODY",BODY,{"disambiguationData":[OSD([sQuery(id+"F0.wireOp",EDGE,"E0"),sQuery(id+"F0.wireOp",EDGE,"E3.filletArc"),sQuery(id+"F0.wireOp",EDGE,"E5"),sQuery(id+"F0.wireOp",EDGE,"E6.MirrorCS")])]});
            var Q1;
            Q1=sQuery(id+"F8.wireOp",EDGE,"E19");
            circularPattern(context, id + "F9", {"entities" : qUnion([Q0]), "axis" : qUnion([Q1]), "angle" : 360 * degree, "instanceCount" : 36, "equalSpace" : true, "computeTransformsWithoutBuiltin" : true});
        }
        {
            var Q0;
            Q0=makeQuery(id+"F9.opPattern","COPY",BODY,{"derivedFrom":makeQuery(id+"F1.opExtrude","SWEPT_BODY",BODY,{"disambiguationData":[OSD([sQuery(id+"F0.wireOp",EDGE,"E0"),sQuery(id+"F0.wireOp",EDGE,"E3.filletArc"),sQuery(id+"F0.wireOp",EDGE,"E5"),sQuery(id+"F0.wireOp",EDGE,"E6.MirrorCS")])]}),"instanceName":"22"});
            var Q1;
            Q1=makeQuery(id+"F1.opExtrude","SWEPT_BODY",BODY,{"disambiguationData":[OSD([sQuery(id+"F0.wireOp",EDGE,"E0"),sQuery(id+"F0.wireOp",EDGE,"E7")])]});
            var Q2;
            Q2=makeQuery(id+"F9.opPattern","COPY",BODY,{"derivedFrom":makeQuery(id+"F1.opExtrude","SWEPT_BODY",BODY,{"disambiguationData":[OSD([sQuery(id+"F0.wireOp",EDGE,"E0"),sQuery(id+"F0.wireOp",EDGE,"E3.filletArc"),sQuery(id+"F0.wireOp",EDGE,"E5"),sQuery(id+"F0.wireOp",EDGE,"E6.MirrorCS")])]}),"instanceName":"21"});
            var Q3;
            Q3=makeQuery(id+"F9.opPattern","COPY",BODY,{"derivedFrom":makeQuery(id+"F1.opExtrude","SWEPT_BODY",BODY,{"disambiguationData":[OSD([sQuery(id+"F0.wireOp",EDGE,"E0"),sQuery(id+"F0.wireOp",EDGE,"E3.filletArc"),sQuery(id+"F0.wireOp",EDGE,"E5"),sQuery(id+"F0.wireOp",EDGE,"E6.MirrorCS")])]}),"instanceName":"20"});
            var Q4;
            Q4=makeQuery(id+"F9.opPattern","COPY",BODY,{"derivedFrom":makeQuery(id+"F1.opExtrude","SWEPT_BODY",BODY,{"disambiguationData":[OSD([sQuery(id+"F0.wireOp",EDGE,"E0"),sQuery(id+"F0.wireOp",EDGE,"E3.filletArc"),sQuery(id+"F0.wireOp",EDGE,"E5"),sQuery(id+"F0.wireOp",EDGE,"E6.MirrorCS")])]}),"instanceName":"19"});
            var Q5;
            Q5=makeQuery(id+"F9.opPattern","COPY",BODY,{"derivedFrom":makeQuery(id+"F1.opExtrude","SWEPT_BODY",BODY,{"disambiguationData":[OSD([sQuery(id+"F0.wireOp",EDGE,"E0"),sQuery(id+"F0.wireOp",EDGE,"E3.filletArc"),sQuery(id+"F0.wireOp",EDGE,"E5"),sQuery(id+"F0.wireOp",EDGE,"E6.MirrorCS")])]}),"instanceName":"18"});
            var Q6;
            Q6=makeQuery(id+"F9.opPattern","COPY",BODY,{"derivedFrom":makeQuery(id+"F1.opExtrude","SWEPT_BODY",BODY,{"disambiguationData":[OSD([sQuery(id+"F0.wireOp",EDGE,"E0"),sQuery(id+"F0.wireOp",EDGE,"E3.filletArc"),sQuery(id+"F0.wireOp",EDGE,"E5"),sQuery(id+"F0.wireOp",EDGE,"E6.MirrorCS")])]}),"instanceName":"17"});
            var Q7;
            Q7=makeQuery(id+"F9.opPattern","COPY",BODY,{"derivedFrom":makeQuery(id+"F1.opExtrude","SWEPT_BODY",BODY,{"disambiguationData":[OSD([sQuery(id+"F0.wireOp",EDGE,"E0"),sQuery(id+"F0.wireOp",EDGE,"E3.filletArc"),sQuery(id+"F0.wireOp",EDGE,"E5"),sQuery(id+"F0.wireOp",EDGE,"E6.MirrorCS")])]}),"instanceName":"16"});
            var Q8;
            Q8=makeQuery(id+"F9.opPattern","COPY",BODY,{"derivedFrom":makeQuery(id+"F1.opExtrude","SWEPT_BODY",BODY,{"disambiguationData":[OSD([sQuery(id+"F0.wireOp",EDGE,"E0"),sQuery(id+"F0.wireOp",EDGE,"E3.filletArc"),sQuery(id+"F0.wireOp",EDGE,"E5"),sQuery(id+"F0.wireOp",EDGE,"E6.MirrorCS")])]}),"instanceName":"15"});
            var Q9;
            Q9=makeQuery(id+"F9.opPattern","COPY",BODY,{"derivedFrom":makeQuery(id+"F1.opExtrude","SWEPT_BODY",BODY,{"disambiguationData":[OSD([sQuery(id+"F0.wireOp",EDGE,"E0"),sQuery(id+"F0.wireOp",EDGE,"E3.filletArc"),sQuery(id+"F0.wireOp",EDGE,"E5"),sQuery(id+"F0.wireOp",EDGE,"E6.MirrorCS")])]}),"instanceName":"14"});
            var Q10;
            Q10=makeQuery(id+"F9.opPattern","COPY",BODY,{"derivedFrom":makeQuery(id+"F1.opExtrude","SWEPT_BODY",BODY,{"disambiguationData":[OSD([sQuery(id+"F0.wireOp",EDGE,"E0"),sQuery(id+"F0.wireOp",EDGE,"E3.filletArc"),sQuery(id+"F0.wireOp",EDGE,"E5"),sQuery(id+"F0.wireOp",EDGE,"E6.MirrorCS")])]}),"instanceName":"13"});
            var Q11;
            Q11=makeQuery(id+"F9.opPattern","COPY",BODY,{"derivedFrom":makeQuery(id+"F1.opExtrude","SWEPT_BODY",BODY,{"disambiguationData":[OSD([sQuery(id+"F0.wireOp",EDGE,"E0"),sQuery(id+"F0.wireOp",EDGE,"E3.filletArc"),sQuery(id+"F0.wireOp",EDGE,"E5"),sQuery(id+"F0.wireOp",EDGE,"E6.MirrorCS")])]}),"instanceName":"12"});
            var Q12;
            Q12=makeQuery(id+"F9.opPattern","COPY",BODY,{"derivedFrom":makeQuery(id+"F1.opExtrude","SWEPT_BODY",BODY,{"disambiguationData":[OSD([sQuery(id+"F0.wireOp",EDGE,"E0"),sQuery(id+"F0.wireOp",EDGE,"E3.filletArc"),sQuery(id+"F0.wireOp",EDGE,"E5"),sQuery(id+"F0.wireOp",EDGE,"E6.MirrorCS")])]}),"instanceName":"11"});
            var Q13;
            Q13=makeQuery(id+"F9.opPattern","COPY",BODY,{"derivedFrom":makeQuery(id+"F1.opExtrude","SWEPT_BODY",BODY,{"disambiguationData":[OSD([sQuery(id+"F0.wireOp",EDGE,"E0"),sQuery(id+"F0.wireOp",EDGE,"E3.filletArc"),sQuery(id+"F0.wireOp",EDGE,"E5"),sQuery(id+"F0.wireOp",EDGE,"E6.MirrorCS")])]}),"instanceName":"10"});
            var Q14;
            Q14=makeQuery(id+"F9.opPattern","COPY",BODY,{"derivedFrom":makeQuery(id+"F1.opExtrude","SWEPT_BODY",BODY,{"disambiguationData":[OSD([sQuery(id+"F0.wireOp",EDGE,"E0"),sQuery(id+"F0.wireOp",EDGE,"E3.filletArc"),sQuery(id+"F0.wireOp",EDGE,"E5"),sQuery(id+"F0.wireOp",EDGE,"E6.MirrorCS")])]}),"instanceName":"9"});
            var Q15;
            Q15=makeQuery(id+"F9.opPattern","COPY",BODY,{"derivedFrom":makeQuery(id+"F1.opExtrude","SWEPT_BODY",BODY,{"disambiguationData":[OSD([sQuery(id+"F0.wireOp",EDGE,"E0"),sQuery(id+"F0.wireOp",EDGE,"E3.filletArc"),sQuery(id+"F0.wireOp",EDGE,"E5"),sQuery(id+"F0.wireOp",EDGE,"E6.MirrorCS")])]}),"instanceName":"8"});
            var Q16;
            Q16=makeQuery(id+"F9.opPattern","COPY",BODY,{"derivedFrom":makeQuery(id+"F1.opExtrude","SWEPT_BODY",BODY,{"disambiguationData":[OSD([sQuery(id+"F0.wireOp",EDGE,"E0"),sQuery(id+"F0.wireOp",EDGE,"E3.filletArc"),sQuery(id+"F0.wireOp",EDGE,"E5"),sQuery(id+"F0.wireOp",EDGE,"E6.MirrorCS")])]}),"instanceName":"7"});
            var Q17;
            Q17=makeQuery(id+"F9.opPattern","COPY",BODY,{"derivedFrom":makeQuery(id+"F1.opExtrude","SWEPT_BODY",BODY,{"disambiguationData":[OSD([sQuery(id+"F0.wireOp",EDGE,"E0"),sQuery(id+"F0.wireOp",EDGE,"E3.filletArc"),sQuery(id+"F0.wireOp",EDGE,"E5"),sQuery(id+"F0.wireOp",EDGE,"E6.MirrorCS")])]}),"instanceName":"6"});
            var Q18;
            Q18=makeQuery(id+"F9.opPattern","COPY",BODY,{"derivedFrom":makeQuery(id+"F1.opExtrude","SWEPT_BODY",BODY,{"disambiguationData":[OSD([sQuery(id+"F0.wireOp",EDGE,"E0"),sQuery(id+"F0.wireOp",EDGE,"E3.filletArc"),sQuery(id+"F0.wireOp",EDGE,"E5"),sQuery(id+"F0.wireOp",EDGE,"E6.MirrorCS")])]}),"instanceName":"5"});
            var Q19;
            Q19=makeQuery(id+"F9.opPattern","COPY",BODY,{"derivedFrom":makeQuery(id+"F1.opExtrude","SWEPT_BODY",BODY,{"disambiguationData":[OSD([sQuery(id+"F0.wireOp",EDGE,"E0"),sQuery(id+"F0.wireOp",EDGE,"E3.filletArc"),sQuery(id+"F0.wireOp",EDGE,"E5"),sQuery(id+"F0.wireOp",EDGE,"E6.MirrorCS")])]}),"instanceName":"4"});
            var Q20;
            Q20=makeQuery(id+"F9.opPattern","COPY",BODY,{"derivedFrom":makeQuery(id+"F1.opExtrude","SWEPT_BODY",BODY,{"disambiguationData":[OSD([sQuery(id+"F0.wireOp",EDGE,"E0"),sQuery(id+"F0.wireOp",EDGE,"E3.filletArc"),sQuery(id+"F0.wireOp",EDGE,"E5"),sQuery(id+"F0.wireOp",EDGE,"E6.MirrorCS")])]}),"instanceName":"3"});
            var Q21;
            Q21=makeQuery(id+"F9.opPattern","COPY",BODY,{"derivedFrom":makeQuery(id+"F1.opExtrude","SWEPT_BODY",BODY,{"disambiguationData":[OSD([sQuery(id+"F0.wireOp",EDGE,"E0"),sQuery(id+"F0.wireOp",EDGE,"E3.filletArc"),sQuery(id+"F0.wireOp",EDGE,"E5"),sQuery(id+"F0.wireOp",EDGE,"E6.MirrorCS")])]}),"instanceName":"2"});
            var Q22;
            Q22=makeQuery(id+"F9.opPattern","COPY",BODY,{"derivedFrom":makeQuery(id+"F1.opExtrude","SWEPT_BODY",BODY,{"disambiguationData":[OSD([sQuery(id+"F0.wireOp",EDGE,"E0"),sQuery(id+"F0.wireOp",EDGE,"E3.filletArc"),sQuery(id+"F0.wireOp",EDGE,"E5"),sQuery(id+"F0.wireOp",EDGE,"E6.MirrorCS")])]}),"instanceName":"1"});
            var Q23;
            Q23=makeQuery(id+"F1.opExtrude","SWEPT_BODY",BODY,{"disambiguationData":[OSD([sQuery(id+"F0.wireOp",EDGE,"E0"),sQuery(id+"F0.wireOp",EDGE,"E3.filletArc"),sQuery(id+"F0.wireOp",EDGE,"E5"),sQuery(id+"F0.wireOp",EDGE,"E6.MirrorCS")])]});
            var Q24;
            Q24=makeQuery(id+"F9.opPattern","COPY",BODY,{"derivedFrom":makeQuery(id+"F1.opExtrude","SWEPT_BODY",BODY,{"disambiguationData":[OSD([sQuery(id+"F0.wireOp",EDGE,"E0"),sQuery(id+"F0.wireOp",EDGE,"E3.filletArc"),sQuery(id+"F0.wireOp",EDGE,"E5"),sQuery(id+"F0.wireOp",EDGE,"E6.MirrorCS")])]}),"instanceName":"35"});
            var Q25;
            Q25=makeQuery(id+"F9.opPattern","COPY",BODY,{"derivedFrom":makeQuery(id+"F1.opExtrude","SWEPT_BODY",BODY,{"disambiguationData":[OSD([sQuery(id+"F0.wireOp",EDGE,"E0"),sQuery(id+"F0.wireOp",EDGE,"E3.filletArc"),sQuery(id+"F0.wireOp",EDGE,"E5"),sQuery(id+"F0.wireOp",EDGE,"E6.MirrorCS")])]}),"instanceName":"34"});
            var Q26;
            Q26=makeQuery(id+"F9.opPattern","COPY",BODY,{"derivedFrom":makeQuery(id+"F1.opExtrude","SWEPT_BODY",BODY,{"disambiguationData":[OSD([sQuery(id+"F0.wireOp",EDGE,"E0"),sQuery(id+"F0.wireOp",EDGE,"E3.filletArc"),sQuery(id+"F0.wireOp",EDGE,"E5"),sQuery(id+"F0.wireOp",EDGE,"E6.MirrorCS")])]}),"instanceName":"33"});
            var Q27;
            Q27=makeQuery(id+"F9.opPattern","COPY",BODY,{"derivedFrom":makeQuery(id+"F1.opExtrude","SWEPT_BODY",BODY,{"disambiguationData":[OSD([sQuery(id+"F0.wireOp",EDGE,"E0"),sQuery(id+"F0.wireOp",EDGE,"E3.filletArc"),sQuery(id+"F0.wireOp",EDGE,"E5"),sQuery(id+"F0.wireOp",EDGE,"E6.MirrorCS")])]}),"instanceName":"32"});
            var Q28;
            Q28=makeQuery(id+"F9.opPattern","COPY",BODY,{"derivedFrom":makeQuery(id+"F1.opExtrude","SWEPT_BODY",BODY,{"disambiguationData":[OSD([sQuery(id+"F0.wireOp",EDGE,"E0"),sQuery(id+"F0.wireOp",EDGE,"E3.filletArc"),sQuery(id+"F0.wireOp",EDGE,"E5"),sQuery(id+"F0.wireOp",EDGE,"E6.MirrorCS")])]}),"instanceName":"31"});
            var Q29;
            Q29=makeQuery(id+"F9.opPattern","COPY",BODY,{"derivedFrom":makeQuery(id+"F1.opExtrude","SWEPT_BODY",BODY,{"disambiguationData":[OSD([sQuery(id+"F0.wireOp",EDGE,"E0"),sQuery(id+"F0.wireOp",EDGE,"E3.filletArc"),sQuery(id+"F0.wireOp",EDGE,"E5"),sQuery(id+"F0.wireOp",EDGE,"E6.MirrorCS")])]}),"instanceName":"30"});
            var Q30;
            Q30=makeQuery(id+"F9.opPattern","COPY",BODY,{"derivedFrom":makeQuery(id+"F1.opExtrude","SWEPT_BODY",BODY,{"disambiguationData":[OSD([sQuery(id+"F0.wireOp",EDGE,"E0"),sQuery(id+"F0.wireOp",EDGE,"E3.filletArc"),sQuery(id+"F0.wireOp",EDGE,"E5"),sQuery(id+"F0.wireOp",EDGE,"E6.MirrorCS")])]}),"instanceName":"29"});
            var Q31;
            Q31=makeQuery(id+"F9.opPattern","COPY",BODY,{"derivedFrom":makeQuery(id+"F1.opExtrude","SWEPT_BODY",BODY,{"disambiguationData":[OSD([sQuery(id+"F0.wireOp",EDGE,"E0"),sQuery(id+"F0.wireOp",EDGE,"E3.filletArc"),sQuery(id+"F0.wireOp",EDGE,"E5"),sQuery(id+"F0.wireOp",EDGE,"E6.MirrorCS")])]}),"instanceName":"28"});
            var Q32;
            Q32=makeQuery(id+"F9.opPattern","COPY",BODY,{"derivedFrom":makeQuery(id+"F1.opExtrude","SWEPT_BODY",BODY,{"disambiguationData":[OSD([sQuery(id+"F0.wireOp",EDGE,"E0"),sQuery(id+"F0.wireOp",EDGE,"E3.filletArc"),sQuery(id+"F0.wireOp",EDGE,"E5"),sQuery(id+"F0.wireOp",EDGE,"E6.MirrorCS")])]}),"instanceName":"27"});
            var Q33;
            Q33=makeQuery(id+"F9.opPattern","COPY",BODY,{"derivedFrom":makeQuery(id+"F1.opExtrude","SWEPT_BODY",BODY,{"disambiguationData":[OSD([sQuery(id+"F0.wireOp",EDGE,"E0"),sQuery(id+"F0.wireOp",EDGE,"E3.filletArc"),sQuery(id+"F0.wireOp",EDGE,"E5"),sQuery(id+"F0.wireOp",EDGE,"E6.MirrorCS")])]}),"instanceName":"26"});
            var Q34;
            Q34=makeQuery(id+"F9.opPattern","COPY",BODY,{"derivedFrom":makeQuery(id+"F1.opExtrude","SWEPT_BODY",BODY,{"disambiguationData":[OSD([sQuery(id+"F0.wireOp",EDGE,"E0"),sQuery(id+"F0.wireOp",EDGE,"E3.filletArc"),sQuery(id+"F0.wireOp",EDGE,"E5"),sQuery(id+"F0.wireOp",EDGE,"E6.MirrorCS")])]}),"instanceName":"25"});
            var Q35;
            Q35=makeQuery(id+"F9.opPattern","COPY",BODY,{"derivedFrom":makeQuery(id+"F1.opExtrude","SWEPT_BODY",BODY,{"disambiguationData":[OSD([sQuery(id+"F0.wireOp",EDGE,"E0"),sQuery(id+"F0.wireOp",EDGE,"E3.filletArc"),sQuery(id+"F0.wireOp",EDGE,"E5"),sQuery(id+"F0.wireOp",EDGE,"E6.MirrorCS")])]}),"instanceName":"23"});
            var Q36;
            Q36=makeQuery(id+"F9.opPattern","COPY",BODY,{"derivedFrom":makeQuery(id+"F1.opExtrude","SWEPT_BODY",BODY,{"disambiguationData":[OSD([sQuery(id+"F0.wireOp",EDGE,"E0"),sQuery(id+"F0.wireOp",EDGE,"E3.filletArc"),sQuery(id+"F0.wireOp",EDGE,"E5"),sQuery(id+"F0.wireOp",EDGE,"E6.MirrorCS")])]}),"instanceName":"24"});
            booleanBodies(context, id + "F10", {"operationType" : BooleanOperationType.UNION, "tools" : qUnion([Q0, Q1, Q2, Q3, Q4, Q5, Q6, Q7, Q8, Q9, Q10, Q11, Q12, Q13, Q14, Q15, Q16, Q17, Q18, Q19, Q20, Q21, Q22, Q23, Q24, Q25, Q26, Q27, Q28, Q29, Q30, Q31, Q32, Q33, Q34, Q35, Q36])});
        }
        {
            var Q0;
            {var subQ0=sQuery(id+"F0.wireOp",EDGE,"E0");var subQ1=makeQuery(id+"F1.opExtrude","CAP_FACE",FACE,{"disambiguationData":[OSD([subQ0,sQuery(id+"F0.wireOp",EDGE,"E3.filletArc"),sQuery(id+"F0.wireOp",EDGE,"E5"),sQuery(id+"F0.wireOp",EDGE,"E6.MirrorCS")])],"isStart":false});Q0=makeQuery(id+"F10.opBoolean","MERGE",FACE,{"derivedFrom":[subQ1,makeQuery(id+"F1.opExtrude","CAP_FACE",FACE,{"disambiguationData":[OSD([subQ0,sQuery(id+"F0.wireOp",EDGE,"E7")])],"isStart":false}),makeQuery(id+"F9.opPattern","COPY",FACE,{"derivedFrom":subQ1,"instanceName":"1"}),makeQuery(id+"F9.opPattern","COPY",FACE,{"derivedFrom":subQ1,"instanceName":"2"}),makeQuery(id+"F9.opPattern","COPY",FACE,{"derivedFrom":subQ1,"instanceName":"3"}),makeQuery(id+"F9.opPattern","COPY",FACE,{"derivedFrom":subQ1,"instanceName":"4"}),makeQuery(id+"F9.opPattern","COPY",FACE,{"derivedFrom":subQ1,"instanceName":"5"}),makeQuery(id+"F9.opPattern","COPY",FACE,{"derivedFrom":subQ1,"instanceName":"6"}),makeQuery(id+"F9.opPattern","COPY",FACE,{"derivedFrom":subQ1,"instanceName":"7"}),makeQuery(id+"F9.opPattern","COPY",FACE,{"derivedFrom":subQ1,"instanceName":"8"}),makeQuery(id+"F9.opPattern","COPY",FACE,{"derivedFrom":subQ1,"instanceName":"9"}),makeQuery(id+"F9.opPattern","COPY",FACE,{"derivedFrom":subQ1,"instanceName":"10"}),makeQuery(id+"F9.opPattern","COPY",FACE,{"derivedFrom":subQ1,"instanceName":"11"}),makeQuery(id+"F9.opPattern","COPY",FACE,{"derivedFrom":subQ1,"instanceName":"12"}),makeQuery(id+"F9.opPattern","COPY",FACE,{"derivedFrom":subQ1,"instanceName":"13"}),makeQuery(id+"F9.opPattern","COPY",FACE,{"derivedFrom":subQ1,"instanceName":"14"}),makeQuery(id+"F9.opPattern","COPY",FACE,{"derivedFrom":subQ1,"instanceName":"15"}),makeQuery(id+"F9.opPattern","COPY",FACE,{"derivedFrom":subQ1,"instanceName":"16"}),makeQuery(id+"F9.opPattern","COPY",FACE,{"derivedFrom":subQ1,"instanceName":"17"}),makeQuery(id+"F9.opPattern","COPY",FACE,{"derivedFrom":subQ1,"instanceName":"18"}),makeQuery(id+"F9.opPattern","COPY",FACE,{"derivedFrom":subQ1,"instanceName":"19"}),makeQuery(id+"F9.opPattern","COPY",FACE,{"derivedFrom":subQ1,"instanceName":"20"}),makeQuery(id+"F9.opPattern","COPY",FACE,{"derivedFrom":subQ1,"instanceName":"21"}),makeQuery(id+"F9.opPattern","COPY",FACE,{"derivedFrom":subQ1,"instanceName":"22"}),makeQuery(id+"F9.opPattern","COPY",FACE,{"derivedFrom":subQ1,"instanceName":"23"}),makeQuery(id+"F9.opPattern","COPY",FACE,{"derivedFrom":subQ1,"instanceName":"24"}),makeQuery(id+"F9.opPattern","COPY",FACE,{"derivedFrom":subQ1,"instanceName":"25"}),makeQuery(id+"F9.opPattern","COPY",FACE,{"derivedFrom":subQ1,"instanceName":"26"}),makeQuery(id+"F9.opPattern","COPY",FACE,{"derivedFrom":subQ1,"instanceName":"27"}),makeQuery(id+"F9.opPattern","COPY",FACE,{"derivedFrom":subQ1,"instanceName":"28"}),makeQuery(id+"F9.opPattern","COPY",FACE,{"derivedFrom":subQ1,"instanceName":"29"}),makeQuery(id+"F9.opPattern","COPY",FACE,{"derivedFrom":subQ1,"instanceName":"30"}),makeQuery(id+"F9.opPattern","COPY",FACE,{"derivedFrom":subQ1,"instanceName":"31"}),makeQuery(id+"F9.opPattern","COPY",FACE,{"derivedFrom":subQ1,"instanceName":"32"}),makeQuery(id+"F9.opPattern","COPY",FACE,{"derivedFrom":subQ1,"instanceName":"33"}),makeQuery(id+"F9.opPattern","COPY",FACE,{"derivedFrom":subQ1,"instanceName":"34"}),makeQuery(id+"F9.opPattern","COPY",FACE,{"derivedFrom":subQ1,"instanceName":"35"})]});}
            var sketch = newSketch(context, id + "F11", { "sketchPlane" : qUnion([Q0])});
            skCircle(sketch, "E20", {"center": v(-11.5, 0) * mm, "radius": 2 * mm});
            skCircle(sketch, "E21.MirrorC", {"center": v(11.5, 0) * mm, "radius": 2 * mm});
            skSolve(sketch);
        }
        {
            var Q0;
            Q0 = qSketchRegion(id + "F11", true);
            extrude(context, id + "F12", {"entities" : qUnion([Q0]), "operationType" : NewBodyOperationType.REMOVE, "oppositeDirection" : true, "depth" : 25 * mm, "offsetDistance" : 25 * mm});
        }
    });
